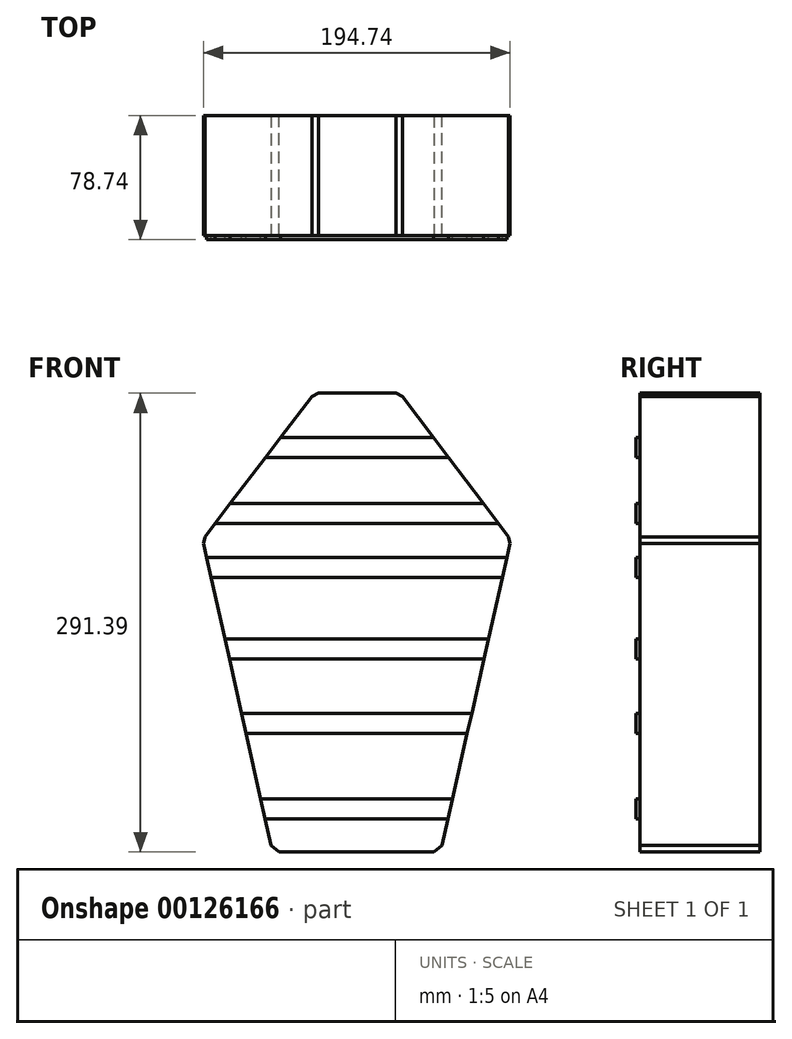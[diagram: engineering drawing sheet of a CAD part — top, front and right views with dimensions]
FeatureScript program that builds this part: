
annotation { "Feature Type Name" : "Feature", "Feature Type Description" : "" }
export const myFeature = defineFeature(function(context is Context, id is Id, definition is map)
    precondition{}
    {
        {
            var Q0;
            Q0=qCreatedBy(makeId("Front.planeOp"),FACE);
            var sketch = newSketch(context, id + "F0", { "sketchPlane" : qUnion([Q0])});
            skLineSegment(sketch, "E0", {"start": v(10.7, 93.17) * mm, "end": v(64.98, 93.17) * mm});
            skLineSegment(sketch, "E1", {"start": v(10.7, 93.17) * mm, "end": v(-60.35, 0) * mm});
            skLineSegment(sketch, "E2", {"start": v(64.98, 93.17) * mm, "end": v(135.43, 0) * mm});
            skLineSegment(sketch, "E3", {"start": v(-60.35, 0) * mm, "end": v(-15.89, -198.22) * mm});
            skLineSegment(sketch, "E4", {"start": v(135.43, 0) * mm, "end": v(90.74, -198.22) * mm});
            skLineSegment(sketch, "E5", {"start": v(-15.89, -198.22) * mm, "end": v(90.74, -198.22) * mm});
            skSolve(sketch);
        }
        {
            var Q0;
            Q0 = qSketchRegion(id + "F0", true);
            extrude(context, id + "F1", {"entities" : qUnion([Q0]), "depth" : 76.2 * mm});
        }
        {
            var Q0;
            Q0=makeQuery(id+"F1.opExtrude","CAP_FACE",FACE,{"disambiguationData":[OSD([sQuery(id+"F0.wireOp",EDGE,"E0"),sQuery(id+"F0.wireOp",EDGE,"E1"),sQuery(id+"F0.wireOp",EDGE,"E2"),sQuery(id+"F0.wireOp",EDGE,"E3"),sQuery(id+"F0.wireOp",EDGE,"E4"),sQuery(id+"F0.wireOp",EDGE,"E5")])],"isStart":false});
            var sketch = newSketch(context, id + "F2", { "sketchPlane" : qUnion([Q0])});
            skLineSegment(sketch, "E6", {"start": v(-10.76, 65.02) * mm, "end": v(86.26, 65.02) * mm});
            skLineSegment(sketch, "E7", {"start": v(86.26, 65.02) * mm, "end": v(95.87, 52.32) * mm});
            skLineSegment(sketch, "E8", {"start": v(95.87, 52.32) * mm, "end": v(-20.44, 52.32) * mm});
            skLineSegment(sketch, "E9", {"start": v(-10.76, 65.02) * mm, "end": v(-20.44, 52.32) * mm});
            skLineSegment(sketch, "E10", {"start": v(-42.85, 22.95) * mm, "end": v(118.08, 22.95) * mm});
            skLineSegment(sketch, "E11", {"start": v(118.08, 22.95) * mm, "end": v(127.68, 10.25) * mm});
            skLineSegment(sketch, "E12", {"start": v(127.68, 10.25) * mm, "end": v(-52.53, 10.25) * mm});
            skLineSegment(sketch, "E13", {"start": v(-42.85, 22.95) * mm, "end": v(-52.53, 10.25) * mm});
            skLineSegment(sketch, "E14", {"start": v(-55, -23.85) * mm, "end": v(130.06, -23.85) * mm});
            skLineSegment(sketch, "E15", {"start": v(-57.85, -11.15) * mm, "end": v(132.92, -11.15) * mm});
            skLineSegment(sketch, "E16", {"start": v(132.92, -11.15) * mm, "end": v(130.06, -23.85) * mm});
            skLineSegment(sketch, "E17", {"start": v(-57.85, -11.15) * mm, "end": v(-55, -23.85) * mm});
            skLineSegment(sketch, "E18", {"start": v(-46.24, -62.89) * mm, "end": v(121.25, -62.89) * mm});
            skLineSegment(sketch, "E19", {"start": v(121.25, -62.89) * mm, "end": v(118.4, -75.59) * mm});
            skLineSegment(sketch, "E20", {"start": v(118.4, -75.59) * mm, "end": v(-43.4, -75.59) * mm});
            skLineSegment(sketch, "E21", {"start": v(-43.4, -75.59) * mm, "end": v(-46.24, -62.89) * mm});
            skLineSegment(sketch, "E22", {"start": v(-35.61, -110.28) * mm, "end": v(110.57, -110.28) * mm});
            skLineSegment(sketch, "E23", {"start": v(110.57, -110.28) * mm, "end": v(107.7, -122.98) * mm});
            skLineSegment(sketch, "E24", {"start": v(107.7, -122.98) * mm, "end": v(-32.77, -122.98) * mm});
            skLineSegment(sketch, "E25", {"start": v(-32.77, -122.98) * mm, "end": v(-35.61, -110.28) * mm});
            skLineSegment(sketch, "E26", {"start": v(-23.45, -164.51) * mm, "end": v(98.34, -164.51) * mm});
            skLineSegment(sketch, "E27", {"start": v(98.34, -164.51) * mm, "end": v(95.48, -177.21) * mm});
            skLineSegment(sketch, "E28", {"start": v(95.48, -177.21) * mm, "end": v(-20.6, -177.21) * mm});
            skLineSegment(sketch, "E29", {"start": v(-20.6, -177.21) * mm, "end": v(-23.45, -164.51) * mm});
            skSolve(sketch);
        }
        {
            var Q0;
            Q0 = qSketchRegion(id + "F2", true);
            extrude(context, id + "F3", {"entities" : qUnion([Q0]), "depth" : 2.54 * mm});
        }
        {
            var Q0;
            Q0=makeQuery(id+"F1.opExtrude","SWEPT_EDGE",EDGE,{"disambiguationData":[OSD([sQuery(id+"F0.wireOp",EDGE,"E1"),sQuery(id+"F0.wireOp",EDGE,"E3")])]});
            var Q1;
            Q1=makeQuery(id+"F1.opExtrude","SWEPT_EDGE",EDGE,{"disambiguationData":[OSD([sQuery(id+"F0.wireOp",EDGE,"E0"),sQuery(id+"F0.wireOp",EDGE,"E1")])]});
            var Q2;
            Q2=makeQuery(id+"F1.opExtrude","SWEPT_EDGE",EDGE,{"disambiguationData":[OSD([sQuery(id+"F0.wireOp",EDGE,"E0"),sQuery(id+"F0.wireOp",EDGE,"E2")])]});
            var Q3;
            Q3=makeQuery(id+"F1.opExtrude","SWEPT_EDGE",EDGE,{"disambiguationData":[OSD([sQuery(id+"F0.wireOp",EDGE,"E2"),sQuery(id+"F0.wireOp",EDGE,"E4")])]});
            var Q4;
            Q4=makeQuery(id+"F1.opExtrude","SWEPT_EDGE",EDGE,{"disambiguationData":[OSD([sQuery(id+"F0.wireOp",EDGE,"E4"),sQuery(id+"F0.wireOp",EDGE,"E5")])]});
            var Q5;
            Q5=makeQuery(id+"F1.opExtrude","SWEPT_EDGE",EDGE,{"disambiguationData":[OSD([sQuery(id+"F0.wireOp",EDGE,"E3"),sQuery(id+"F0.wireOp",EDGE,"E5")])]});
            chamfer(context, id + "F4", {"entities" : qUnion([Q0, Q1, Q2, Q3, Q4, Q5]), "width" : 5.08 * mm, "tangentPropagation" : true});
        }
    });
